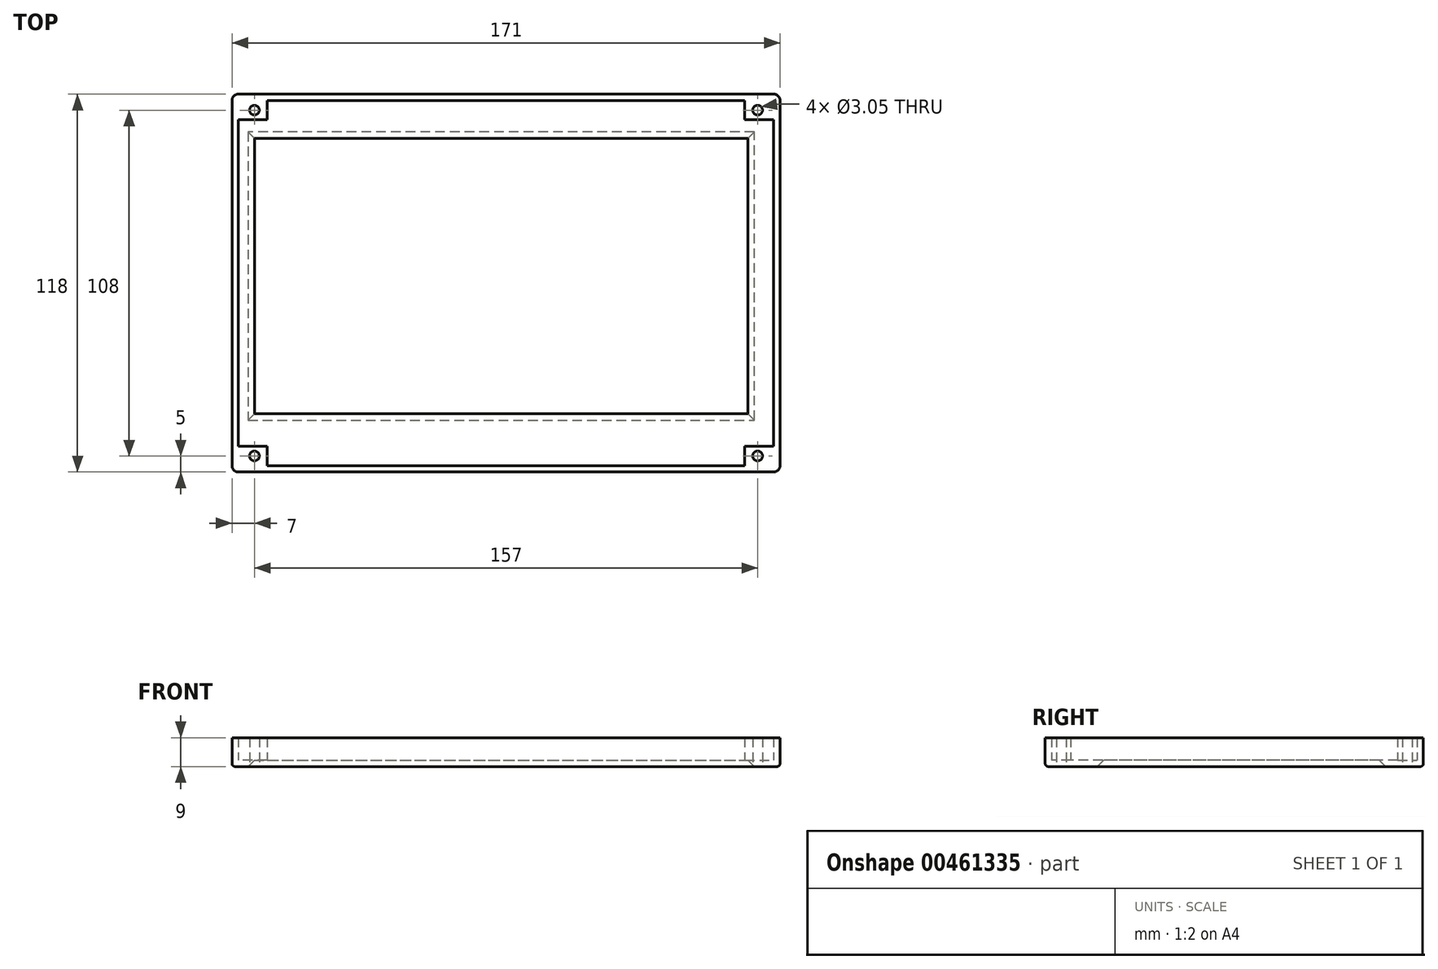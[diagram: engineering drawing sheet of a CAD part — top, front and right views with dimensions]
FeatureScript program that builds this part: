
annotation { "Feature Type Name" : "Feature", "Feature Type Description" : "" }
export const myFeature = defineFeature(function(context is Context, id is Id, definition is map)
    precondition{}
    {
        {
            var Q0;
            Q0=qCreatedBy(makeId("Top.planeOp"),FACE);
            var sketch = newSketch(context, id + "F0", { "sketchPlane" : qUnion([Q0])});
            skLineSegment(sketch, "E0.bottom", {"start": v(-84.75, 57.9) * mm, "end": v(86.25, 57.9) * mm});
            skLineSegment(sketch, "E0.top", {"start": v(-84.75, -60.11) * mm, "end": v(86.25, -60.11) * mm});
            skLineSegment(sketch, "E0.left", {"start": v(-84.75, 57.9) * mm, "end": v(-84.75, -60.11) * mm});
            skLineSegment(sketch, "E0.right", {"start": v(86.25, 57.9) * mm, "end": v(86.25, -60.11) * mm});
            skLineSegment(sketch, "E1.bottom", {"start": v(-77.75, 44.11) * mm, "end": v(76.25, 44.11) * mm});
            skLineSegment(sketch, "E1.top", {"start": v(-77.75, -41.9) * mm, "end": v(76.25, -41.9) * mm});
            skLineSegment(sketch, "E1.left", {"start": v(-77.75, 44.11) * mm, "end": v(-77.75, -41.9) * mm});
            skLineSegment(sketch, "E1.right", {"start": v(76.25, 44.11) * mm, "end": v(76.25, -41.9) * mm});
            skSolve(sketch);
        }
        {
            var Q0;
            Q0=makeQuery(id+"F0.imprint","IMPRINT",FACE,{"disambiguationData":[TD([[makeQuery(id+"F0.imprint","IMPRINT",EDGE,{"derivedFrom":sQuery(id+"F0.wireOp",EDGE,"E0.bottom")}),-1.0]])]});
            extrude(context, id + "F1", {"entities" : qUnion([Q0]), "oppositeDirection" : true, "depth" : 2 * mm});
        }
        {
            var Q0;
            Q0=makeQuery(id+"F1.opExtrude","CAP_EDGE",EDGE,{"disambiguationData":[OSD([sQuery(id+"F0.wireOp",EDGE,"E1.right")])],"isStart":false});
            var Q1;
            Q1=makeQuery(id+"F1.opExtrude","CAP_EDGE",EDGE,{"disambiguationData":[OSD([sQuery(id+"F0.wireOp",EDGE,"E1.top")])],"isStart":false});
            var Q2;
            Q2=makeQuery(id+"F1.opExtrude","CAP_EDGE",EDGE,{"disambiguationData":[OSD([sQuery(id+"F0.wireOp",EDGE,"E1.bottom")])],"isStart":false});
            var Q3;
            Q3=makeQuery(id+"F1.opExtrude","CAP_EDGE",EDGE,{"disambiguationData":[OSD([sQuery(id+"F0.wireOp",EDGE,"E1.left")])],"isStart":false});
            chamfer(context, id + "F2", {"entities" : qUnion([Q0, Q1, Q2, Q3]), "width" : 2 * mm, "tangentPropagation" : true});
        }
        {
            var Q0;
            Q0=makeQuery(id+"F1.opExtrude","CAP_EDGE",EDGE,{"disambiguationData":[OSD([sQuery(id+"F0.wireOp",EDGE,"E0.left")])],"isStart":false});
            var Q1;
            Q1=makeQuery(id+"F1.opExtrude","CAP_EDGE",EDGE,{"disambiguationData":[OSD([sQuery(id+"F0.wireOp",EDGE,"E0.top")])],"isStart":false});
            var Q2;
            Q2=makeQuery(id+"F1.opExtrude","CAP_EDGE",EDGE,{"disambiguationData":[OSD([sQuery(id+"F0.wireOp",EDGE,"E0.right")])],"isStart":false});
            var Q3;
            Q3=makeQuery(id+"F1.opExtrude","CAP_EDGE",EDGE,{"disambiguationData":[OSD([sQuery(id+"F0.wireOp",EDGE,"E0.bottom")])],"isStart":false});
            fillet(context, id + "F3", {"entities" : qUnion([Q0, Q1, Q2, Q3]), "radius" : 1 * mm, "tangentPropagation" : true, "allowEdgeOverflow" : false});
        }
        {
            var Q0;
            Q0=makeQuery(id+"F1.opExtrude","CAP_FACE",FACE,{"disambiguationData":[OSD([sQuery(id+"F0.wireOp",EDGE,"E0.bottom"),sQuery(id+"F0.wireOp",EDGE,"E0.top"),sQuery(id+"F0.wireOp",EDGE,"E0.left"),sQuery(id+"F0.wireOp",EDGE,"E0.right"),sQuery(id+"F0.wireOp",EDGE,"E1.bottom"),sQuery(id+"F0.wireOp",EDGE,"E1.top"),sQuery(id+"F0.wireOp",EDGE,"E1.left"),sQuery(id+"F0.wireOp",EDGE,"E1.right")])],"isStart":true});
            var sketch = newSketch(context, id + "F4", { "sketchPlane" : qUnion([Q0])});
            skLineSegment(sketch, "E2.bottom", {"start": v(-82.75, 55.9) * mm, "end": v(84.25, 55.9) * mm});
            skLineSegment(sketch, "E2.top", {"start": v(-82.75, -58.1) * mm, "end": v(84.25, -58.1) * mm});
            skLineSegment(sketch, "E2.left", {"start": v(-82.75, 55.9) * mm, "end": v(-82.75, -58.1) * mm});
            skLineSegment(sketch, "E2.right", {"start": v(84.25, 55.9) * mm, "end": v(84.25, -58.1) * mm});
            skSolve(sketch);
        }
        {
            var Q0;
            Q0=makeQuery(id+"F4.imprint","IMPRINT",FACE,{"disambiguationData":[TD([[makeQuery(id+"F4.imprint","IMPRINT",EDGE,{"derivedFrom":sQuery(id+"F4.wireOp",EDGE,"E2.bottom")}),1.0]])]});
            extrude(context, id + "F5", {"entities" : qUnion([Q0]), "operationType" : NewBodyOperationType.ADD, "depth" : 7 * mm});
        }
        {
            var Q0;
            Q0=makeQuery(id+"F1.opExtrude","CAP_FACE",FACE,{"disambiguationData":[OSD([sQuery(id+"F0.wireOp",EDGE,"E0.bottom"),sQuery(id+"F0.wireOp",EDGE,"E0.top"),sQuery(id+"F0.wireOp",EDGE,"E0.left"),sQuery(id+"F0.wireOp",EDGE,"E0.right"),sQuery(id+"F0.wireOp",EDGE,"E1.bottom"),sQuery(id+"F0.wireOp",EDGE,"E1.top"),sQuery(id+"F0.wireOp",EDGE,"E1.left"),sQuery(id+"F0.wireOp",EDGE,"E1.right")])],"isStart":true});
            var sketch = newSketch(context, id + "F6", { "sketchPlane" : qUnion([Q0])});
            skLineSegment(sketch, "E3.bottom", {"start": v(-82.75, 55.9) * mm, "end": v(-73.75, 55.9) * mm});
            skLineSegment(sketch, "E3.top", {"start": v(-82.75, 49.9) * mm, "end": v(-73.75, 49.9) * mm});
            skLineSegment(sketch, "E3.left", {"start": v(-82.75, 55.9) * mm, "end": v(-82.75, 49.9) * mm});
            skLineSegment(sketch, "E3.right", {"start": v(-73.75, 55.9) * mm, "end": v(-73.75, 49.9) * mm});
            skLineSegment(sketch, "E4.bottom", {"start": v(75.25, 49.9) * mm, "end": v(84.25, 49.9) * mm});
            skLineSegment(sketch, "E4.top", {"start": v(75.25, 55.9) * mm, "end": v(84.25, 55.9) * mm});
            skLineSegment(sketch, "E4.left", {"start": v(75.25, 49.9) * mm, "end": v(75.25, 55.9) * mm});
            skLineSegment(sketch, "E4.right", {"start": v(84.25, 49.9) * mm, "end": v(84.25, 55.9) * mm});
            skLineSegment(sketch, "E5.bottom", {"start": v(75.25, -52.1) * mm, "end": v(84.25, -52.1) * mm});
            skLineSegment(sketch, "E5.top", {"start": v(75.25, -58.1) * mm, "end": v(84.25, -58.1) * mm});
            skLineSegment(sketch, "E5.left", {"start": v(75.25, -52.1) * mm, "end": v(75.25, -58.1) * mm});
            skLineSegment(sketch, "E5.right", {"start": v(84.25, -52.1) * mm, "end": v(84.25, -58.1) * mm});
            skPoint(sketch, "E6.firstSnap0", {"position": v(79.75, -52.1) * mm});
            skLineSegment(sketch, "E6.bottom", {"start": v(-73.75, -52.1) * mm, "end": v(-82.75, -52.1) * mm});
            skLineSegment(sketch, "E6.top", {"start": v(-73.75, -58.1) * mm, "end": v(-82.75, -58.1) * mm});
            skLineSegment(sketch, "E6.left", {"start": v(-73.75, -52.1) * mm, "end": v(-73.75, -58.1) * mm});
            skLineSegment(sketch, "E6.right", {"start": v(-82.75, -52.1) * mm, "end": v(-82.75, -58.1) * mm});
            skSolve(sketch);
        }
        {
            var Q0;
            Q0=makeQuery(id+"F6.imprint","IMPRINT",FACE,{"disambiguationData":[TD([[makeQuery(id+"F6.imprint","IMPRINT",EDGE,{"derivedFrom":sQuery(id+"F6.wireOp",EDGE,"E3.bottom")}),-1.0]])]});
            var Q1;
            Q1=makeQuery(id+"F6.imprint","IMPRINT",FACE,{"disambiguationData":[TD([[makeQuery(id+"F6.imprint","IMPRINT",EDGE,{"derivedFrom":sQuery(id+"F6.wireOp",EDGE,"E4.bottom")}),1.0]])]});
            var Q2;
            Q2=makeQuery(id+"F6.imprint","IMPRINT",FACE,{"disambiguationData":[TD([[makeQuery(id+"F6.imprint","IMPRINT",EDGE,{"derivedFrom":sQuery(id+"F6.wireOp",EDGE,"E5.bottom")}),-1.0]])]});
            var Q3;
            Q3=makeQuery(id+"F6.imprint","IMPRINT",FACE,{"disambiguationData":[TD([[makeQuery(id+"F6.imprint","IMPRINT",EDGE,{"derivedFrom":sQuery(id+"F6.wireOp",EDGE,"E6.bottom")}),1.0]])]});
            extrude(context, id + "F7", {"entities" : qUnion([Q0, Q1, Q2, Q3]), "operationType" : NewBodyOperationType.ADD, "depth" : 7 * mm});
        }
        {
            var Q0;
            Q0=makeQuery(id+"F1.opExtrude","CAP_FACE",FACE,{"disambiguationData":[OSD([sQuery(id+"F0.wireOp",EDGE,"E0.bottom"),sQuery(id+"F0.wireOp",EDGE,"E0.top"),sQuery(id+"F0.wireOp",EDGE,"E0.left"),sQuery(id+"F0.wireOp",EDGE,"E0.right"),sQuery(id+"F0.wireOp",EDGE,"E1.bottom"),sQuery(id+"F0.wireOp",EDGE,"E1.top"),sQuery(id+"F0.wireOp",EDGE,"E1.left"),sQuery(id+"F0.wireOp",EDGE,"E1.right")])],"isStart":false});
            var sketch = newSketch(context, id + "F8", { "sketchPlane" : qUnion([Q0])});
            skCircle(sketch, "E7", {"center": v(-77.75, 55.11) * mm, "radius": 1.52 * mm});
            skCircle(sketch, "E8", {"center": v(79.25, 55.11) * mm, "radius": 1.52 * mm});
            skCircle(sketch, "E9", {"center": v(79.25, -52.9) * mm, "radius": 1.53 * mm});
            skCircle(sketch, "E10", {"center": v(-77.75, -52.9) * mm, "radius": 1.52 * mm});
            skSolve(sketch);
        }
        {
            var Q0;
            Q0=makeQuery(id+"F8.imprint","IMPRINT",FACE,{"disambiguationData":[TD([[makeQuery(id+"F8.imprint","IMPRINT",EDGE,{"derivedFrom":sQuery(id+"F8.wireOp",EDGE,"E7")}),1.0]])]});
            var Q1;
            Q1=makeQuery(id+"F8.imprint","IMPRINT",FACE,{"disambiguationData":[TD([[makeQuery(id+"F8.imprint","IMPRINT",EDGE,{"derivedFrom":sQuery(id+"F8.wireOp",EDGE,"E8")}),1.0]])]});
            var Q2;
            Q2=makeQuery(id+"F8.imprint","IMPRINT",FACE,{"disambiguationData":[TD([[makeQuery(id+"F8.imprint","IMPRINT",EDGE,{"derivedFrom":sQuery(id+"F8.wireOp",EDGE,"E10")}),1.0]])]});
            var Q3;
            Q3=makeQuery(id+"F8.imprint","IMPRINT",FACE,{"disambiguationData":[TD([[makeQuery(id+"F8.imprint","IMPRINT",EDGE,{"derivedFrom":sQuery(id+"F8.wireOp",EDGE,"E9")}),1.0]])]});
            extrude(context, id + "F9", {"entities" : qUnion([Q0, Q1, Q2, Q3]), "operationType" : NewBodyOperationType.REMOVE, "endBound" : BoundingType.THROUGH_ALL, "oppositeDirection" : true, "depth" : 25 * mm});
        }
        {
            var Q0;
            {var subQ0=sQuery(id+"F0.wireOp",EDGE,"E0.left");var subQ1=sQuery(id+"F0.wireOp",EDGE,"E0.bottom");Q0=makeQuery(id+"F5.boolean.opBoolean","MERGE",EDGE,{"derivedFrom":[makeQuery(id+"F1.opExtrude","SWEPT_EDGE",EDGE,{"disambiguationData":[OSD([subQ1,subQ0])]}),makeQuery(id+"F5.opExtrude","SWEPT_EDGE",EDGE,{"disambiguationData":[OSD([subQ1,subQ0])]})]});}
            var Q1;
            {var subQ0=sQuery(id+"F0.wireOp",EDGE,"E0.right");var subQ1=sQuery(id+"F0.wireOp",EDGE,"E0.bottom");Q1=makeQuery(id+"F5.boolean.opBoolean","MERGE",EDGE,{"derivedFrom":[makeQuery(id+"F1.opExtrude","SWEPT_EDGE",EDGE,{"disambiguationData":[OSD([subQ1,subQ0])]}),makeQuery(id+"F5.opExtrude","SWEPT_EDGE",EDGE,{"disambiguationData":[OSD([subQ1,subQ0])]})]});}
            var Q2;
            {var subQ0=sQuery(id+"F0.wireOp",EDGE,"E0.right");var subQ1=sQuery(id+"F0.wireOp",EDGE,"E0.top");Q2=makeQuery(id+"F5.boolean.opBoolean","MERGE",EDGE,{"derivedFrom":[makeQuery(id+"F1.opExtrude","SWEPT_EDGE",EDGE,{"disambiguationData":[OSD([subQ1,subQ0])]}),makeQuery(id+"F5.opExtrude","SWEPT_EDGE",EDGE,{"disambiguationData":[OSD([subQ1,subQ0])]})]});}
            var Q3;
            {var subQ0=sQuery(id+"F0.wireOp",EDGE,"E0.left");var subQ1=sQuery(id+"F0.wireOp",EDGE,"E0.top");Q3=makeQuery(id+"F5.boolean.opBoolean","MERGE",EDGE,{"derivedFrom":[makeQuery(id+"F1.opExtrude","SWEPT_EDGE",EDGE,{"disambiguationData":[OSD([subQ1,subQ0])]}),makeQuery(id+"F5.opExtrude","SWEPT_EDGE",EDGE,{"disambiguationData":[OSD([subQ1,subQ0])]})]});}
            fillet(context, id + "F10", {"entities" : qUnion([Q0, Q1, Q2, Q3]), "radius" : 2 * mm, "tangentPropagation" : true, "allowEdgeOverflow" : false});
        }
    });
